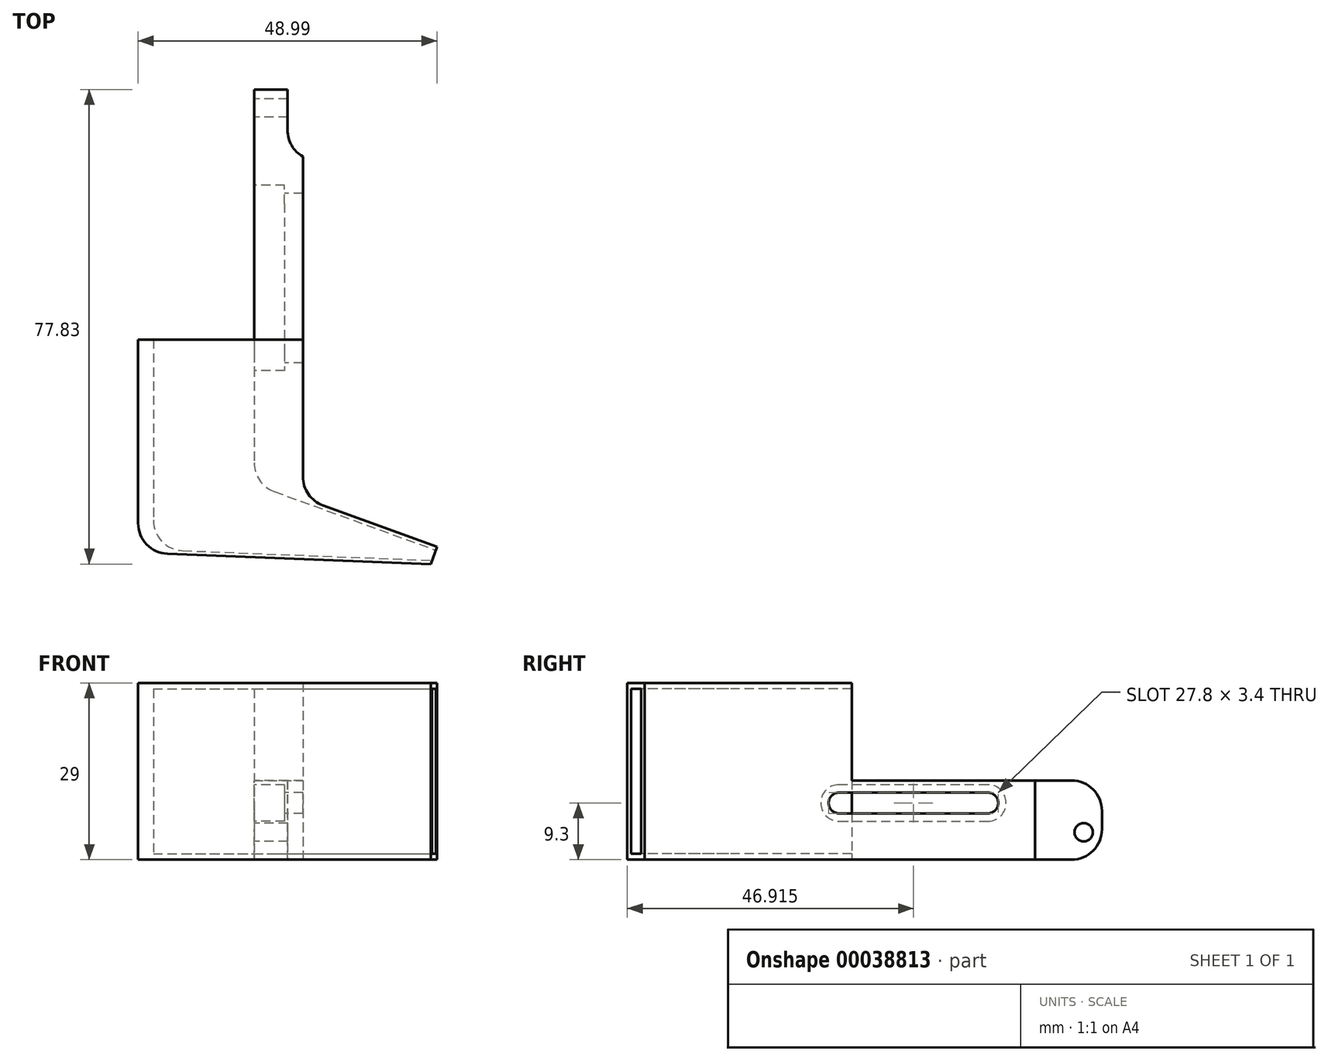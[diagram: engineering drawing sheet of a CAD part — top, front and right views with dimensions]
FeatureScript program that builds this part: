
annotation { "Feature Type Name" : "Feature", "Feature Type Description" : "" }
export const myFeature = defineFeature(function(context is Context, id is Id, definition is map)
    precondition{}
    {
        {
            var Q0;
            Q0=qCreatedBy(makeId("Top.planeOp"),FACE);
            var sketch = newSketch(context, id + "F0", { "sketchPlane" : qUnion([Q0])});
            skLineSegment(sketch, "E0", {"start": v(0, 0) * mm, "end": v(0, 34.96) * mm});
            skLineSegment(sketch, "E1", {"start": v(0, 34.96) * mm, "end": v(27, 34.96) * mm});
            skLineSegment(sketch, "E2", {"start": v(27, 34.96) * mm, "end": v(27, 8.96) * mm});
            skLineSegment(sketch, "E3", {"start": v(27, 8.96) * mm, "end": v(48.99, 0.95) * mm});
            skLineSegment(sketch, "E4", {"start": v(48.99, 0.95) * mm, "end": v(47.96, -1.87) * mm});
            skLineSegment(sketch, "E5", {"start": v(47.96, -1.87) * mm, "end": v(0, 0) * mm});
            skSolve(sketch);
        }
        {
            var Q0;
            Q0=qSketchRegion(id+"F0",true);
            extrude(context, id + "F1", {"entities" : qUnion([Q0]), "depth" : 1 * mm});
        }
        {
            var Q0;
            Q0=makeQuery(id+"F1.opExtrude","CAP_FACE",FACE,{"disambiguationData":[OSD([sQuery(id+"F0.wireOp",EDGE,"E0"),sQuery(id+"F0.wireOp",EDGE,"E1"),sQuery(id+"F0.wireOp",EDGE,"E2"),sQuery(id+"F0.wireOp",EDGE,"E3"),sQuery(id+"F0.wireOp",EDGE,"E4"),sQuery(id+"F0.wireOp",EDGE,"E5")])],"isStart":false});
            var sketch = newSketch(context, id + "F2", { "sketchPlane" : qUnion([Q0])});
            skLineSegment(sketch, "E6", {"start": v(0, 34.96) * mm, "end": v(2.5, 34.96) * mm});
            skLineSegment(sketch, "E7", {"start": v(2.5, 34.96) * mm, "end": v(2.5, 0.5) * mm});
            skLineSegment(sketch, "E8", {"start": v(2.5, 0.5) * mm, "end": v(48.18, -1.27) * mm});
            skLineSegment(sketch, "E9", {"start": v(48.18, -1.27) * mm, "end": v(47.96, -1.87) * mm});
            skLineSegment(sketch, "E10", {"start": v(27, 34.96) * mm, "end": v(19, 34.96) * mm});
            skLineSegment(sketch, "E11", {"start": v(19, 34.96) * mm, "end": v(19, 11.23) * mm});
            skLineSegment(sketch, "E12", {"start": v(19, 11.23) * mm, "end": v(48.78, 0.4) * mm});
            skSolve(sketch);
        }
        {
            var Q0;
            Q0=qSketchRegion(id+"F2",true);
            var Q1;
            Q1=makeQuery(id+"F2.imprint","IMPRINT",FACE,{"disambiguationData":[TD([[makeQuery(id+"F2.imprint","IMPRINT",EDGE,{"derivedFrom":sQuery(id+"F2.wireOp",EDGE,"E6")}),-1.0]])]});
            var Q2;
            Q2=makeQuery(id+"F2.imprint","IMPRINT",FACE,{"disambiguationData":[TD([[makeQuery(id+"F2.imprint","IMPRINT",EDGE,{"derivedFrom":sQuery(id+"F2.wireOp",EDGE,"E10")}),-1.0]])]});
            extrude(context, id + "F3", {"entities" : qUnion([Q0, Q1, Q2]), "operationType" : NewBodyOperationType.ADD, "depth" : 27 * mm});
        }
        {
            var Q0;
            Q0=makeQuery(id+"F3.opExtrude","CAP_FACE",FACE,{"disambiguationData":[OSD([sQuery(id+"F0.wireOp",EDGE,"E2"),sQuery(id+"F0.wireOp",EDGE,"E3"),sQuery(id+"F0.wireOp",EDGE,"E4"),sQuery(id+"F2.wireOp",EDGE,"E10"),sQuery(id+"F2.wireOp",EDGE,"E11"),sQuery(id+"F2.wireOp",EDGE,"E12")])],"isStart":false});
            var sketch = newSketch(context, id + "F4", { "sketchPlane" : qUnion([Q0])});
            skLineSegment(sketch, "E13", {"start": v(0, 0) * mm, "end": v(0, 34.96) * mm});
            skLineSegment(sketch, "E14", {"start": v(0, 34.96) * mm, "end": v(27, 34.96) * mm});
            skLineSegment(sketch, "E15", {"start": v(27, 34.96) * mm, "end": v(27, 8.96) * mm});
            skLineSegment(sketch, "E16", {"start": v(27, 8.96) * mm, "end": v(48.99, 0.95) * mm});
            skLineSegment(sketch, "E17", {"start": v(48.99, 0.95) * mm, "end": v(47.96, -1.87) * mm});
            skLineSegment(sketch, "E18", {"start": v(47.96, -1.87) * mm, "end": v(0, 0) * mm});
            skSolve(sketch);
        }
        {
            var Q0;
            Q0=qSketchRegion(id+"F4",true);
            extrude(context, id + "F5", {"entities" : qUnion([Q0]), "operationType" : NewBodyOperationType.ADD, "depth" : 1 * mm});
        }
        {
            var Q0;
            Q0=makeQuery(id+"F1.opExtrude","CAP_FACE",FACE,{"disambiguationData":[OSD([sQuery(id+"F0.wireOp",EDGE,"E0"),sQuery(id+"F0.wireOp",EDGE,"E1"),sQuery(id+"F0.wireOp",EDGE,"E2"),sQuery(id+"F0.wireOp",EDGE,"E3"),sQuery(id+"F0.wireOp",EDGE,"E4"),sQuery(id+"F0.wireOp",EDGE,"E5")])],"isStart":true});
            var sketch = newSketch(context, id + "F6", { "sketchPlane" : qUnion([Q0])});
            skLineSegment(sketch, "E19", {"start": v(27, -34.96) * mm, "end": v(27, -64.96) * mm});
            skLineSegment(sketch, "E20", {"start": v(27, -64.96) * mm, "end": v(24.5, -64.96) * mm});
            skLineSegment(sketch, "E21", {"start": v(24.5, -64.96) * mm, "end": v(24.5, -75.96) * mm});
            skLineSegment(sketch, "E22", {"start": v(24.5, -75.96) * mm, "end": v(19, -75.96) * mm});
            skLineSegment(sketch, "E23", {"start": v(19, -75.96) * mm, "end": v(19, -34.96) * mm});
            skSolve(sketch);
        }
        {
            var Q0;
            Q0=qSketchRegion(id+"F6",true);
            var Q1;
            {var subQ2=sQuery(id+"F6.wireOp",EDGE,"E19");Q1=makeQuery(id+"F6.imprint","IMPRINT",FACE,{"disambiguationData":[TD([[makeQuery(id+"F6.imprint","IMPRINT",EDGE,{"derivedFrom":subQ2}),-1.0]])]});}
            extrude(context, id + "F7", {"entities" : qUnion([Q0, Q1]), "operationType" : NewBodyOperationType.ADD, "oppositeDirection" : true, "depth" : 13 * mm});
        }
        {
            var Q0;
            Q0=makeQuery(id+"F7.boolean.opBoolean","MERGE",FACE,{"derivedFrom":[makeQuery(id+"F3.opExtrude","SWEPT_FACE",FACE,{"disambiguationData":[OSD([sQuery(id+"F2.wireOp",EDGE,"E11")])]}),makeQuery(id+"F7.opExtrude","SWEPT_FACE",FACE,{"disambiguationData":[OSD([sQuery(id+"F6.wireOp",EDGE,"E23")])]})]});
            var sketch = newSketch(context, id + "F8", { "sketchPlane" : qUnion([Q0])});
            skCircle(sketch, "E24", {"center": v(-72.96, 4.5) * mm, "radius": 1.5 * mm});
            skPoint(sketch, "E24.centerSnap0", {"position": v(-75.96, 6.5) * mm});
            skArc(sketch, "E25", {"start": v(-57.25, 11) * mm, "mid": v(-58.95, 9.3) * mm, "end": v(-57.25, 7.6) * mm});
            skArc(sketch, "E26", {"start": v(-32.85, 7.6) * mm, "mid": v(-31.15, 9.3) * mm, "end": v(-32.85, 11) * mm});
            skLineSegment(sketch, "E27", {"start": v(-57.25, 11) * mm, "end": v(-32.85, 11) * mm});
            skLineSegment(sketch, "E28", {"start": v(-57.25, 7.6) * mm, "end": v(-32.85, 7.6) * mm});
            skArc(sketch, "E29", {"start": v(-57.25, 12.3) * mm, "mid": v(-60.25, 9.3) * mm, "end": v(-57.25, 6.3) * mm});
            skArc(sketch, "E30", {"start": v(-32.85, 6.3) * mm, "mid": v(-29.85, 9.3) * mm, "end": v(-32.85, 12.3) * mm});
            skLineSegment(sketch, "E31", {"start": v(-57.25, 12.3) * mm, "end": v(-32.85, 12.3) * mm});
            skLineSegment(sketch, "E32", {"start": v(-32.85, 6.3) * mm, "end": v(-57.25, 6.3) * mm});
            skSolve(sketch);
        }
        {
            var Q0;
            Q0=makeQuery(id+"F8.imprint","IMPRINT",FACE,{"disambiguationData":[TD([[makeQuery(id+"F8.imprint","IMPRINT",EDGE,{"derivedFrom":sQuery(id+"F8.wireOp",EDGE,"E24")}),1.0]])]});
            var Q1;
            Q1=makeQuery(id+"F8.imprint","IMPRINT",FACE,{"disambiguationData":[TD([[makeQuery(id+"F8.imprint","IMPRINT",EDGE,{"derivedFrom":sQuery(id+"F8.wireOp",EDGE,"E25")}),1.0]])]});
            extrude(context, id + "F9", {"entities" : qUnion([Q0, Q1]), "operationType" : NewBodyOperationType.REMOVE, "oppositeDirection" : true, "depth" : 25 * mm});
        }
        {
            var Q0;
            Q0=makeQuery(id+"F8.imprint","IMPRINT",FACE,{"disambiguationData":[TD([[makeQuery(id+"F8.imprint","IMPRINT",EDGE,{"derivedFrom":sQuery(id+"F8.wireOp",EDGE,"E25")}),-1.0]])]});
            extrude(context, id + "F10", {"entities" : qUnion([Q0]), "operationType" : NewBodyOperationType.REMOVE, "oppositeDirection" : true, "depth" : 5 * mm});
        }
        {
            var Q0;
            {var subQ0=sQuery(id+"F0.wireOp",EDGE,"E0");var subQ1=sQuery(id+"F0.wireOp",EDGE,"E5");Q0=makeQuery(id+"F5.boolean.opBoolean","MERGE",EDGE,{"derivedFrom":[makeQuery(id+"F3.boolean.opBoolean","MERGE",EDGE,{"derivedFrom":[makeQuery(id+"F1.opExtrude","SWEPT_EDGE",EDGE,{"disambiguationData":[OSD([subQ0,subQ1])]}),makeQuery(id+"F3.opExtrude","SWEPT_EDGE",EDGE,{"disambiguationData":[OSD([subQ0,subQ1])]})]}),makeQuery(id+"F5.opExtrude","SWEPT_EDGE",EDGE,{"disambiguationData":[OSD([sQuery(id+"F4.wireOp",EDGE,"E13"),sQuery(id+"F4.wireOp",EDGE,"E18")])]})]});}
            var Q1;
            {var subQ0=sQuery(id+"F0.wireOp",EDGE,"E2");var subQ1=sQuery(id+"F0.wireOp",EDGE,"E3");Q1=makeQuery(id+"F5.boolean.opBoolean","MERGE",EDGE,{"derivedFrom":[makeQuery(id+"F3.boolean.opBoolean","MERGE",EDGE,{"derivedFrom":[makeQuery(id+"F1.opExtrude","SWEPT_EDGE",EDGE,{"disambiguationData":[OSD([subQ0,subQ1])]}),makeQuery(id+"F3.opExtrude","SWEPT_EDGE",EDGE,{"disambiguationData":[OSD([subQ0,subQ1])]})]}),makeQuery(id+"F5.opExtrude","SWEPT_EDGE",EDGE,{"disambiguationData":[OSD([sQuery(id+"F4.wireOp",EDGE,"E15"),sQuery(id+"F4.wireOp",EDGE,"E16")])]})]});}
            var Q2;
            Q2=makeQuery(id+"F3.opExtrude","SWEPT_EDGE",EDGE,{"disambiguationData":[OSD([sQuery(id+"F2.wireOp",EDGE,"E7"),sQuery(id+"F2.wireOp",EDGE,"E8")])]});
            var Q3;
            Q3=makeQuery(id+"F3.opExtrude","SWEPT_EDGE",EDGE,{"disambiguationData":[OSD([sQuery(id+"F2.wireOp",EDGE,"E11"),sQuery(id+"F2.wireOp",EDGE,"E12")])]});
            var Q4;
            Q4=makeQuery(id+"F7.opExtrude","SWEPT_EDGE",EDGE,{"disambiguationData":[OSD([sQuery(id+"F6.wireOp",EDGE,"E20"),sQuery(id+"F6.wireOp",EDGE,"E21")])]});
            var Q5;
            Q5=makeQuery(id+"F7.opExtrude","CAP_EDGE",EDGE,{"disambiguationData":[OSD([sQuery(id+"F6.wireOp",EDGE,"E22")])],"isStart":false});
            var Q6;
            Q6=makeQuery(id+"F7.opExtrude","CAP_EDGE",EDGE,{"disambiguationData":[OSD([sQuery(id+"F6.wireOp",EDGE,"E22")])],"isStart":true});
            fillet(context, id + "F11", {"entities" : qUnion([Q0, Q1, Q2, Q3, Q4, Q5, Q6]), "radius" : 5 * mm, "tangentPropagation" : true, "allowEdgeOverflow" : false});
        }
    });
